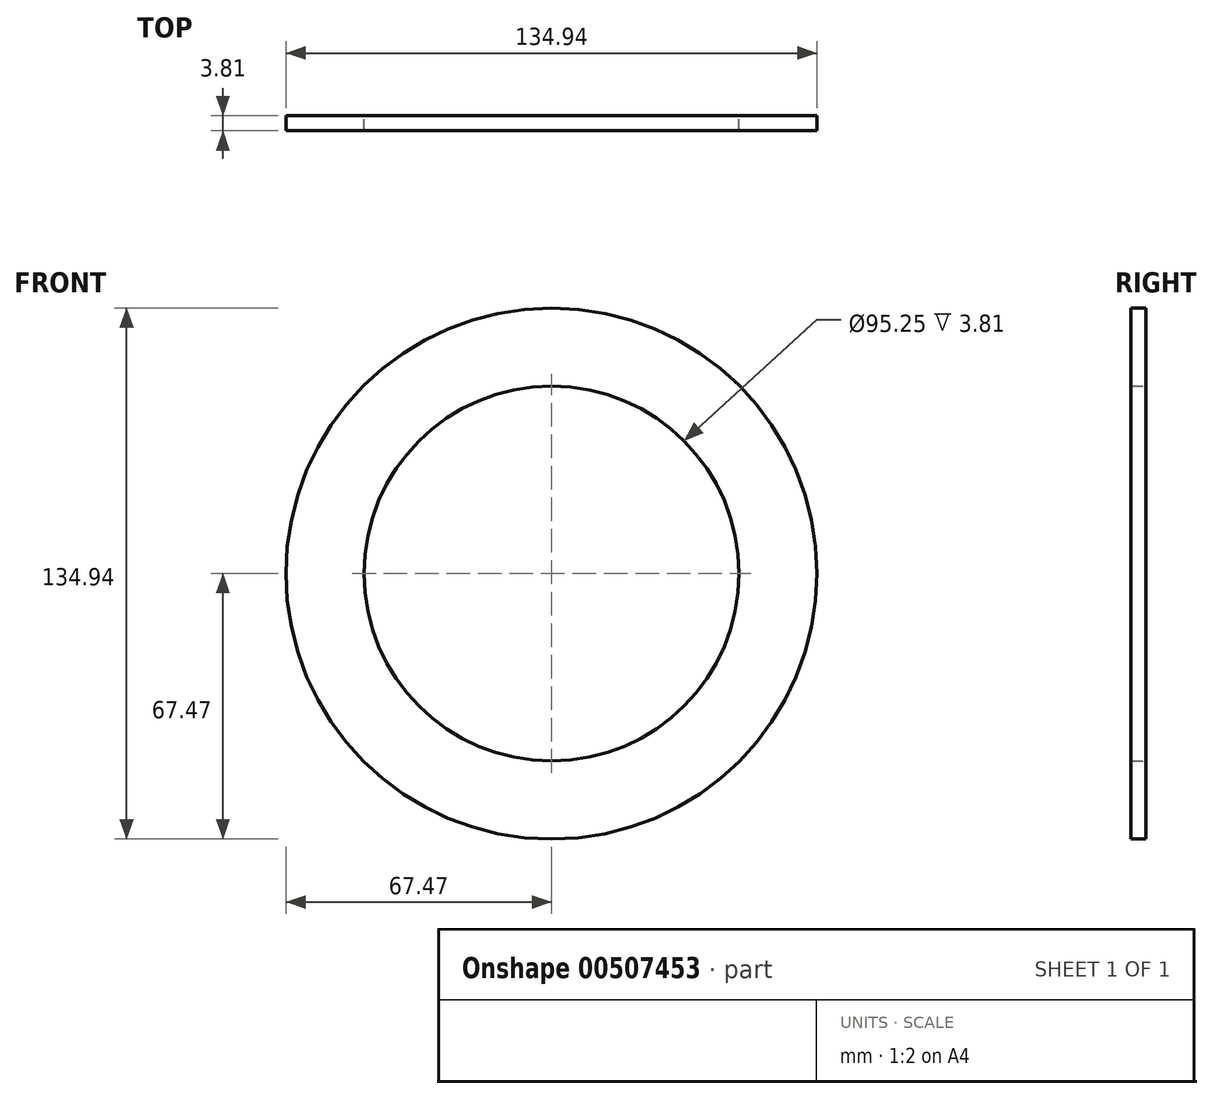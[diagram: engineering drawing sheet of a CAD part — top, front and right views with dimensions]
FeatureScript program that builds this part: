
annotation { "Feature Type Name" : "Feature", "Feature Type Description" : "" }
export const myFeature = defineFeature(function(context is Context, id is Id, definition is map)
    precondition{}
    {
        {
            var Q0;
            Q0=qCreatedBy(makeId("Front.planeOp"),FACE);
            var sketch = newSketch(context, id + "F0", { "sketchPlane" : qUnion([Q0])});
            skCircle(sketch, "E0", {"center": v(0, 0) * mm, "radius": 47.63 * mm});
            skCircle(sketch, "E1", {"center": v(0, 0) * mm, "radius": 67.47 * mm});
            skSolve(sketch);
        }
        {
            var Q0;
            Q0=makeQuery(id+"F0.imprint","IMPRINT",FACE,{"disambiguationData":[TD([[makeQuery(id+"F0.imprint","IMPRINT",EDGE,{"derivedFrom":sQuery(id+"F0.wireOp",EDGE,"E0")}),-1.0]])]});
            extrude(context, id + "F1", {"entities" : qUnion([Q0]), "depth" : 3.8 * mm});
        }
    });
